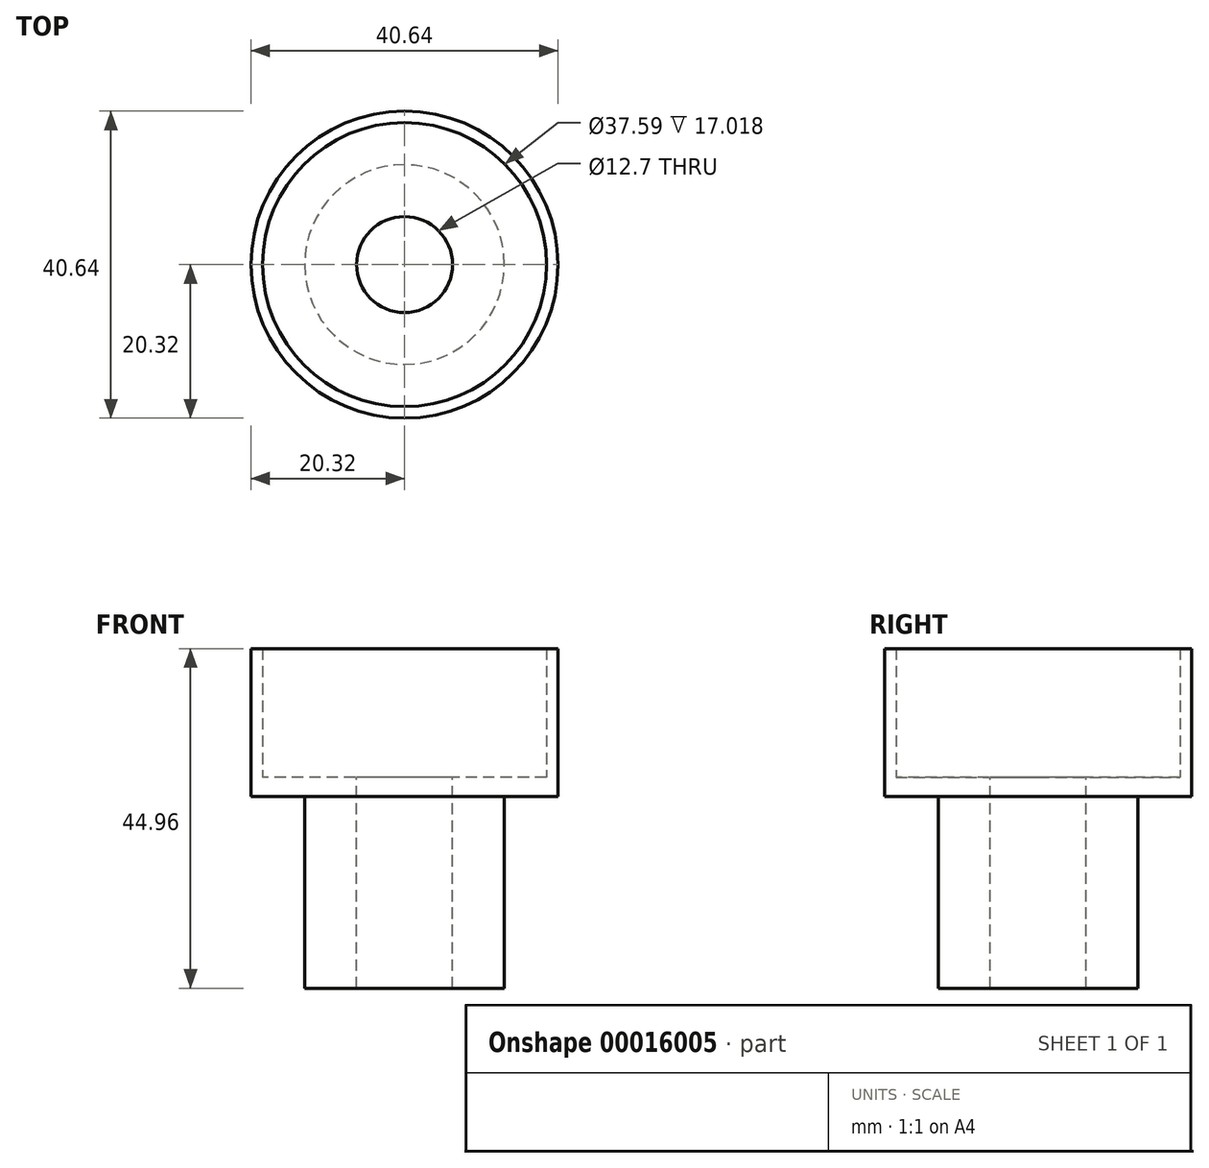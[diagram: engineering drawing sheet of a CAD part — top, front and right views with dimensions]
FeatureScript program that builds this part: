
annotation { "Feature Type Name" : "Feature", "Feature Type Description" : "" }
export const myFeature = defineFeature(function(context is Context, id is Id, definition is map)
    precondition{}
    {
        {
            var Q0;
            Q0=qCreatedBy(makeId("Top.planeOp"),FACE);
            var sketch = newSketch(context, id + "F0", { "sketchPlane" : qUnion([Q0])});
            skCircle(sketch, "E0", {"center": v(0, 0) * mm, "radius": 13.22 * mm});
            skSolve(sketch);
        }
        {
            var Q0;
            Q0 = qSketchRegion(id + "F0", true);
            extrude(context, id + "F1", {"entities" : qUnion([Q0]), "depth" : 25.4 * mm});
        }
        {
            var Q0;
            Q0=makeQuery(id+"F1.opExtrude","CAP_FACE",FACE,{"disambiguationData":[OSD([sQuery(id+"F0.wireOp",EDGE,"E0")])],"isStart":false});
            var sketch = newSketch(context, id + "F2", { "sketchPlane" : qUnion([Q0])});
            skCircle(sketch, "E1", {"center": v(0, 0) * mm, "radius": 20.32 * mm});
            skSolve(sketch);
        }
        {
            var Q0;
            Q0 = qSketchRegion(id + "F2", true);
            extrude(context, id + "F3", {"entities" : qUnion([Q0]), "operationType" : NewBodyOperationType.ADD, "depth" : 2.54 * mm});
        }
        {
            var Q0;
            Q0=makeQuery(id+"F3.opExtrude","CAP_FACE",FACE,{"disambiguationData":[OSD([sQuery(id+"F2.wireOp",EDGE,"E1")])],"isStart":false});
            var sketch = newSketch(context, id + "F4", { "sketchPlane" : qUnion([Q0])});
            skCircle(sketch, "E2", {"center": v(0, 0) * mm, "radius": 20.32 * mm});
            skCircle(sketch, "E3", {"center": v(0, 0) * mm, "radius": 18.8 * mm});
            skSolve(sketch);
        }
        {
            var Q0;
            Q0=makeQuery(id+"F4.imprint","IMPRINT",FACE,{"disambiguationData":[TD([[makeQuery(id+"F4.imprint","IMPRINT",EDGE,{"derivedFrom":sQuery(id+"F4.wireOp",EDGE,"E2")}),1.0]])]});
            extrude(context, id + "F5", {"entities" : qUnion([Q0]), "operationType" : NewBodyOperationType.ADD, "depth" : 17.02 * mm});
        }
        {
            var Q0;
            Q0=makeQuery(id+"F3.opExtrude","CAP_FACE",FACE,{"disambiguationData":[OSD([sQuery(id+"F2.wireOp",EDGE,"E1")])],"isStart":false});
            var sketch = newSketch(context, id + "F6", { "sketchPlane" : qUnion([Q0])});
            skCircle(sketch, "E4", {"center": v(0, 0) * mm, "radius": 6.35 * mm});
            skSolve(sketch);
        }
        {
            var Q0;
            Q0 = qSketchRegion(id + "F6", true);
            extrude(context, id + "F7", {"entities" : qUnion([Q0]), "operationType" : NewBodyOperationType.REMOVE, "oppositeDirection" : true, "depth" : 31.77 * mm});
        }
    });
